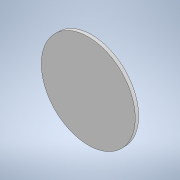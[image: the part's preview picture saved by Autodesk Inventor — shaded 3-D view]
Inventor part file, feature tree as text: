
AUTODESK INVENTOR PART (.ipt)
format: ipt  version: 2021 (Build 250183000, 183)  size: 92,160 bytes
history: native  units: mm
features: extrude x1, sketch x1
ambient origin geometry x8: Origin, YZ Plane, XZ Plane, XY Plane, X Axis, Y Axis, Z Axis, Center Point
bodies: Solide1 (feature_tree)
feature tree (2):
  extrude  "Extrusion1"  Depth=54.5mm
  sketch  "Esquisse1"
